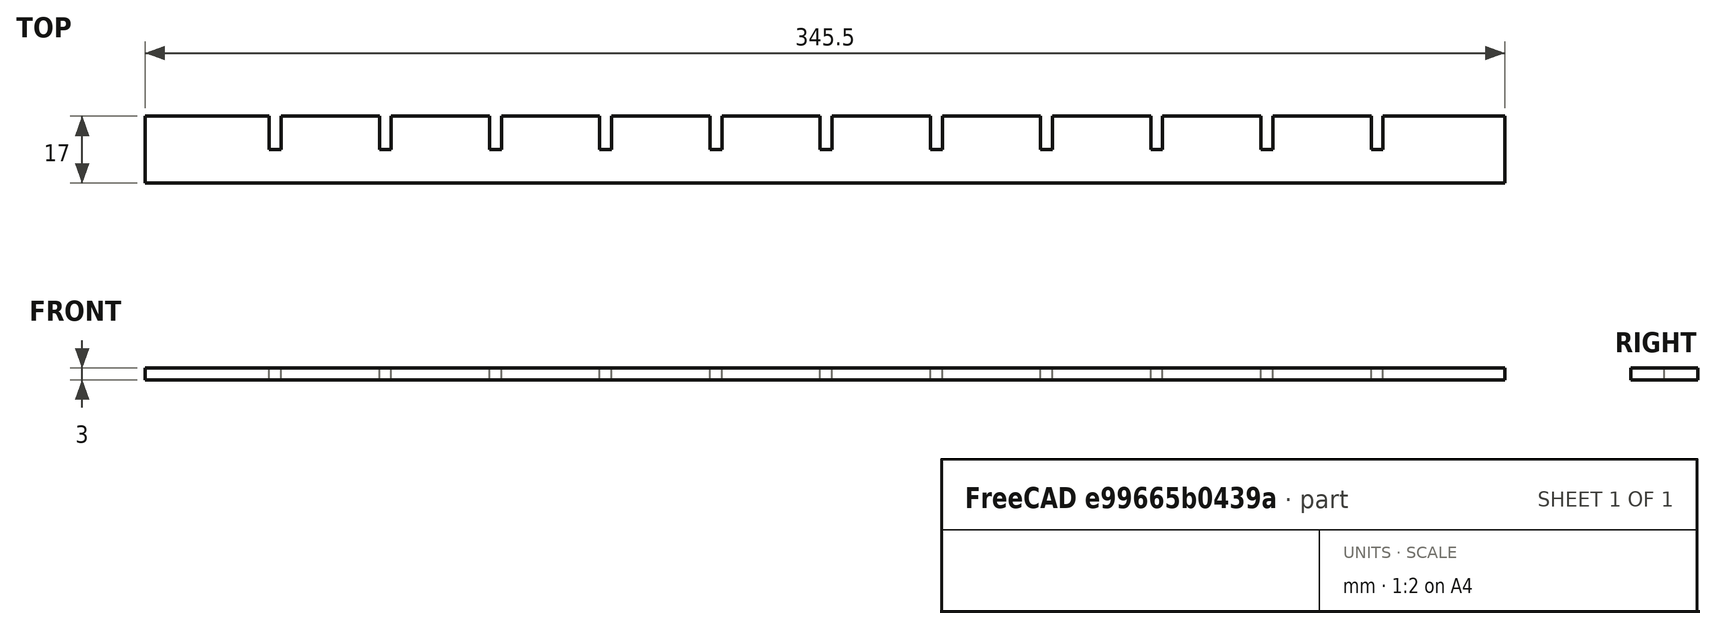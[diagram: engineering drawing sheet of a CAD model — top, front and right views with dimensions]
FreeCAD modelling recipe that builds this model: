
FCSTD DOCUMENT  (FreeCAD 0.16R6706 (Git))
Label: Leiste_kurz_ohneAufnahme_12x
License: All rights reserved
LicenseURL: http://de.wikipedia.org/wiki/Alle_Rechte_vorbehalten
objects: Sketcher::SketchObject×1, PartDesign::Pad×1
note: 3 computed .brp shape members not serialized (recipe doc carries the construction recipe); baked Part::Feature solids carry a one-line shape summary decoded from their .brp

FEATURE [Sketcher::SketchObject] Sketch
  sketch-geometry (48):
    g0: LineSegment StartX=0 StartY=0 StartZ=0 EndX=0 EndY=17 EndZ=0
    g1: LineSegment StartX=0 StartY=17 StartZ=0 EndX=31.5 EndY=17 EndZ=0
    g2: LineSegment StartX=31.5 StartY=17 StartZ=0 EndX=31.5 EndY=8.5 EndZ=0
    g3: LineSegment StartX=31.5 StartY=8.5 StartZ=0 EndX=34.5 EndY=8.5 EndZ=0
    g4: LineSegment StartX=34.5 StartY=8.5 StartZ=0 EndX=34.5 EndY=17 EndZ=0
    g5: LineSegment StartX=34.5 StartY=17 StartZ=0 EndX=59.5 EndY=17 EndZ=0
    g6: LineSegment StartX=59.5 StartY=17 StartZ=0 EndX=59.5 EndY=8.5 EndZ=0
    g7: LineSegment StartX=59.5 StartY=8.5 StartZ=0 EndX=62.5 EndY=8.5 EndZ=0
    g8: LineSegment StartX=62.5 StartY=8.5 StartZ=0 EndX=62.5 EndY=17 EndZ=0
    g9: LineSegment StartX=62.5 StartY=17 StartZ=0 EndX=87.5 EndY=17 EndZ=0
    g10: LineSegment StartX=87.5 StartY=17 StartZ=0 EndX=87.5 EndY=8.5 EndZ=0
    g11: LineSegment StartX=87.5 StartY=8.5 StartZ=0 EndX=90.5 EndY=8.5 EndZ=0
    g12: LineSegment StartX=90.5 StartY=8.5 StartZ=0 EndX=90.5 EndY=17 EndZ=0
    g13: LineSegment StartX=90.5 StartY=17 StartZ=0 EndX=115.5 EndY=17 EndZ=0
    g14: LineSegment StartX=115.5 StartY=17 StartZ=0 EndX=115.5 EndY=8.5 EndZ=0
    g15: LineSegment StartX=115.5 StartY=8.5 StartZ=0 EndX=118.5 EndY=8.5 EndZ=0
    g16: LineSegment StartX=118.5 StartY=8.5 StartZ=0 EndX=118.5 EndY=17 EndZ=0
    g17: LineSegment StartX=118.5 StartY=17 StartZ=0 EndX=143.5 EndY=17 EndZ=0
    g18: LineSegment StartX=143.5 StartY=17 StartZ=0 EndX=143.5 EndY=8.5 EndZ=0
    g19: LineSegment StartX=143.5 StartY=8.5 StartZ=0 EndX=146.5 EndY=8.5 EndZ=0
    g20: LineSegment StartX=146.5 StartY=8.5 StartZ=0 EndX=146.5 EndY=17 EndZ=0
    g21: LineSegment StartX=146.5 StartY=17 StartZ=0 EndX=171.5 EndY=17 EndZ=0
    g22: LineSegment StartX=171.5 StartY=17 StartZ=0 EndX=171.5 EndY=8.5 EndZ=0
    g23: LineSegment StartX=171.5 StartY=8.5 StartZ=0 EndX=174.5 EndY=8.5 EndZ=0
    g24: LineSegment StartX=174.5 StartY=8.5 StartZ=0 EndX=174.5 EndY=17 EndZ=0
    g25: LineSegment StartX=174.5 StartY=17 StartZ=0 EndX=199.5 EndY=17 EndZ=0
    g26: LineSegment StartX=199.5 StartY=17 StartZ=0 EndX=199.5 EndY=8.5 EndZ=0
    g27: LineSegment StartX=199.5 StartY=8.5 StartZ=0 EndX=202.5 EndY=8.5 EndZ=0
    g28: LineSegment StartX=202.5 StartY=8.5 StartZ=0 EndX=202.5 EndY=17 EndZ=0
    g29: LineSegment StartX=202.5 StartY=17 StartZ=0 EndX=227.5 EndY=17 EndZ=0
    g30: LineSegment StartX=227.5 StartY=17 StartZ=0 EndX=227.5 EndY=8.5 EndZ=0
    g31: LineSegment StartX=227.5 StartY=8.5 StartZ=0 EndX=230.5 EndY=8.5 EndZ=0
    g32: LineSegment StartX=230.5 StartY=8.5 StartZ=0 EndX=230.5 EndY=17 EndZ=0
    g33: LineSegment StartX=230.5 StartY=17 StartZ=0 EndX=255.5 EndY=17 EndZ=0
    g34: LineSegment StartX=255.5 StartY=17 StartZ=0 EndX=255.5 EndY=8.5 EndZ=0
    g35: LineSegment StartX=255.5 StartY=8.5 StartZ=0 EndX=258.5 EndY=8.5 EndZ=0
    g36: LineSegment StartX=258.5 StartY=8.5 StartZ=0 EndX=258.5 EndY=17 EndZ=0
    g37: LineSegment StartX=258.5 StartY=17 StartZ=0 EndX=283.5 EndY=17 EndZ=0
    g38: LineSegment StartX=283.5 StartY=17 StartZ=0 EndX=283.5 EndY=8.5 EndZ=0
    g39: LineSegment StartX=283.5 StartY=8.5 StartZ=0 EndX=286.5 EndY=8.5 EndZ=0
    g40: LineSegment StartX=286.5 StartY=8.5 StartZ=0 EndX=286.5 EndY=17 EndZ=0
    g41: LineSegment StartX=286.5 StartY=17 StartZ=0 EndX=311.5 EndY=17 EndZ=0
    g42: LineSegment StartX=311.5 StartY=17 StartZ=0 EndX=311.5 EndY=8.5 EndZ=0
    g43: LineSegment StartX=311.5 StartY=8.5 StartZ=0 EndX=314.5 EndY=8.5 EndZ=0
    g44: LineSegment StartX=314.5 StartY=8.5 StartZ=0 EndX=314.5 EndY=17 EndZ=0
    g45: LineSegment StartX=314.5 StartY=17 StartZ=0 EndX=345.5 EndY=17 EndZ=0
    g46: LineSegment StartX=345.5 StartY=17 StartZ=0 EndX=345.5 EndY=0 EndZ=0
    g47: LineSegment StartX=345.5 StartY=0 StartZ=0 EndX=0 EndY=0 EndZ=0
  constraints (143):
    c: Coincident(g-1,g0)
    c: PointOnObject(g0,g-2)
    c: Coincident(g0,g1)
    c: Horizontal(g1)
    c: Coincident(g1,g2)
    c: Vertical(g2)
    c: Coincident(g2,g3)
    c: Horizontal(g3)
    c: Coincident(g3,g4)
    c: Vertical(g4)
    c: Coincident(g4,g5)
    c: Horizontal(g5)
    c: DistanceX(g2,g3) = 3
    c: DistanceX(g1,g5) = 28
    c: DistanceY(g2,g1) = 8.5
    c: Equal(g2,g4)
    c: Coincident(g5,g6)
    c: Vertical(g6)
    c: Coincident(g6,g7)
    c: Horizontal(g7)
    c: Coincident(g7,g8)
    c: Vertical(g8)
    c: Coincident(g8,g9)
    c: Horizontal(g9)
    c: Coincident(g9,g10)
    c: Vertical(g10)
    c: Coincident(g10,g11)
    c: Horizontal(g11)
    c: Coincident(g11,g12)
    c: Vertical(g12)
    c: Coincident(g12,g13)
    c: Horizontal(g13)
    c: Coincident(g13,g14)
    c: Vertical(g14)
    c: Coincident(g14,g15)
    c: Horizontal(g15)
    c: Coincident(g15,g16)
    c: Vertical(g16)
    c: Coincident(g16,g17)
    c: Horizontal(g17)
    c: Coincident(g17,g18)
    c: Vertical(g18)
    c: Coincident(g18,g19)
    c: Horizontal(g19)
    c: Coincident(g19,g20)
    c: Vertical(g20)
    c: Coincident(g20,g21)
    c: Horizontal(g21)
    c: Coincident(g21,g22)
    c: Vertical(g22)
    c: Coincident(g22,g23)
    c: Horizontal(g23)
    c: Coincident(g23,g24)
    c: Vertical(g24)
    c: Coincident(g24,g25)
    c: Horizontal(g25)
    c: Coincident(g25,g26)
    c: Vertical(g26)
    c: Coincident(g26,g27)
    c: Horizontal(g27)
    c: Coincident(g27,g28)
    c: Vertical(g28)
    c: Coincident(g28,g29)
    c: Horizontal(g29)
    c: Coincident(g29,g30)
    c: Vertical(g30)
    c: Coincident(g30,g31)
    c: Horizontal(g31)
    c: Coincident(g31,g32)
    c: Vertical(g32)
    c: Coincident(g32,g33)
    c: Horizontal(g33)
    c: Coincident(g33,g34)
    c: Vertical(g34)
    c: Coincident(g34,g35)
    c: Horizontal(g35)
    c: Coincident(g35,g36)
    c: Vertical(g36)
    c: Coincident(g36,g37)
    c: Horizontal(g37)
    c: Coincident(g37,g38)
    c: Vertical(g38)
    c: Coincident(g38,g39)
    c: Horizontal(g39)
    c: Coincident(g39,g40)
    c: Vertical(g40)
    c: Coincident(g40,g41)
    c: Horizontal(g41)
    c: Coincident(g41,g42)
    c: Vertical(g42)
    c: Coincident(g42,g43)
    c: Horizontal(g43)
    c: Coincident(g43,g44)
    c: Vertical(g44)
    c: Horizontal(g45)
    c: Coincident(g45,g46)
    c: Vertical(g46)
    c: Coincident(g46,g47)
    c: Coincident(g47,g-1)
    c: Horizontal(g47)
    c: Equal(g4,g6)
    c: Equal(g6,g8)
    c: Equal(g8,g10)
    c: Equal(g10,g12)
    c: Equal(g12,g14)
    c: Equal(g14,g16)
    c: Equal(g16,g18)
    c: Equal(g18,g20)
    c: Equal(g20,g22)
    c: Equal(g22,g24)
    c: Equal(g24,g26)
    c: Equal(g26,g28)
    c: Equal(g28,g30)
    c: Equal(g30,g32)
    c: Equal(g32,g34)
    c: Equal(g34,g36)
    c: Equal(g36,g38)
    c: Equal(g38,g40)
    c: Equal(g40,g42)
    c: Equal(g42,g44)
    c: Equal(g5,g9)
    c: Equal(g9,g13)
    c: Equal(g3,g7)
    c: Equal(g7,g11)
    c: DistanceX(g-1,g46) = 345.5
    c: Equal(g13,g17)
    c: Equal(g17,g21)
    c: Equal(g11,g15)
    c: Equal(g15,g19)
    c: Equal(g21,g25)
    c: Equal(g25,g29)
    c: Equal(g19,g23)
    c: Equal(g23,g27)
    c: Equal(g29,g33)
    c: Equal(g33,g37)
    c: Equal(g37,g41)
    c: Equal(g27,g31)
    c: Equal(g31,g35)
    c: Equal(g35,g39)
    c: Equal(g39,g43)
    c: DistanceY(g-1,g0) = 17
    c: DistanceX(g0,g1) = 31.5
    c: Coincident(g44,g45)
FEATURE [PartDesign::Pad] Pad
  Length = 3
  Length2 = 100
  Sketch = -> Sketch
  Type = 0
